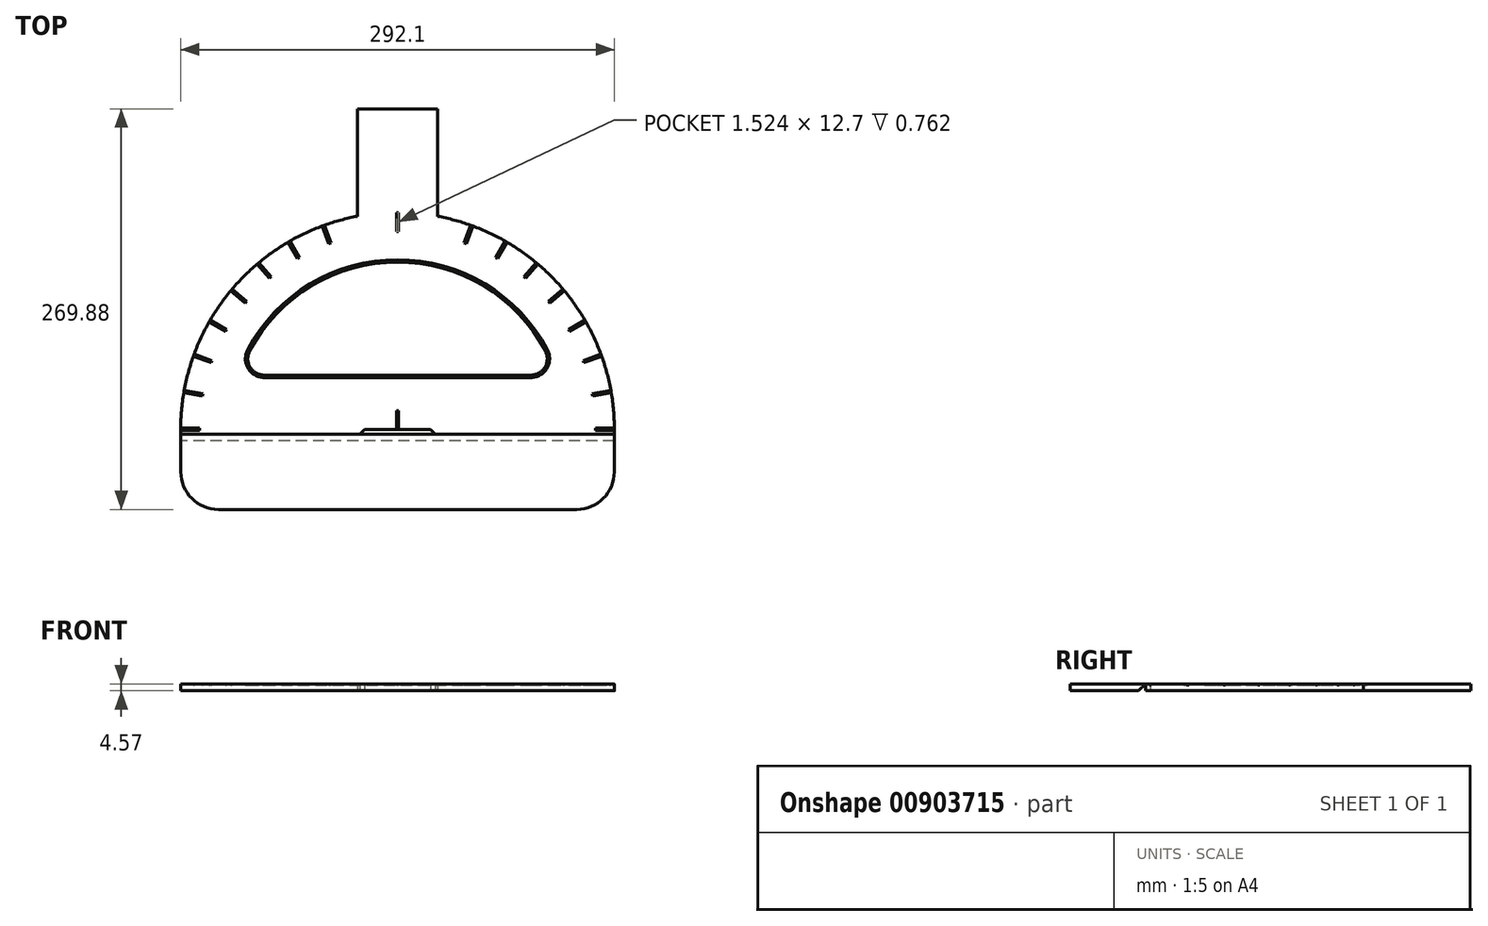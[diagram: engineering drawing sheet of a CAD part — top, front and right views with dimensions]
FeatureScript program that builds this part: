
annotation { "Feature Type Name" : "Feature", "Feature Type Description" : "" }
export const myFeature = defineFeature(function(context is Context, id is Id, definition is map)
    precondition{}
    {
        {
            var Q0;
            Q0=qCreatedBy(makeId("Top.planeOp"),FACE);
            var sketch = newSketch(context, id + "F0", { "sketchPlane" : qUnion([Q0])});
            skArc(sketch, "E0", {"start": v(146.02, -3.17) * mm, "mid": v(113.44, 92) * mm, "end": v(27.05, 143.52) * mm});
            skLineSegment(sketch, "E1", {"start": v(-146.02, -3.18) * mm, "end": v(-25.4, -3.18) * mm});
            skLineSegment(sketch, "E2", {"start": v(-25.4, -3.18) * mm, "end": v(-22.22, 0) * mm});
            skLineSegment(sketch, "E3", {"start": v(0, 4.34) * mm, "end": v(0, -10.16) * mm, "construction": true});
            skLineSegment(sketch, "E4.MirrorCS", {"start": v(25.4, -3.18) * mm, "end": v(22.22, 0) * mm});
            skLineSegment(sketch, "E5", {"start": v(-22.22, 0) * mm, "end": v(22.22, 0) * mm});
            skLineSegment(sketch, "E6.trimOffspring", {"start": v(25.4, -3.18) * mm, "end": v(146.02, -3.18) * mm});
            skLineSegment(sketch, "E7", {"start": v(0, 220.1) * mm, "end": v(0, 0) * mm, "construction": true});
            skLineSegment(sketch, "E8.bottom", {"start": v(-27.05, 215.9) * mm, "end": v(27.05, 215.9) * mm});
            skLineSegment(sketch, "E8.left", {"start": v(-27.05, 215.9) * mm, "end": v(-27.05, 143.52) * mm});
            skLineSegment(sketch, "E8.right", {"start": v(27.05, 215.9) * mm, "end": v(27.05, 143.52) * mm});
            skArc(sketch, "E9.trimOffspring", {"start": v(-27.05, 143.52) * mm, "mid": v(-113.44, 92) * mm, "end": v(-146.02, -3.17) * mm});
            skSolve(sketch);
        }
        {
            var Q0;
            Q0 = qSketchRegion(id + "F0", true);
            extrude(context, id + "F1", {"entities" : qUnion([Q0]), "depth" : 4.57 * mm, "offsetDistance" : 25.4 * mm});
        }
        {
            var Q0;
            Q0=makeQuery(id+"F1.opExtrude","CAP_FACE",FACE,{"disambiguationData":[OSD([sQuery(id+"F0.wireOp",EDGE,"E0"),sQuery(id+"F0.wireOp",EDGE,"E1")])],"isStart":false});
            var sketch = newSketch(context, id + "F2", { "sketchPlane" : qUnion([Q0])});
            skLineSegment(sketch, "E10", {"start": v(-89.75, 34.92) * mm, "end": v(89.75, 34.92) * mm});
            skArc(sketch, "E11.0", {"start": v(100.96, 53.58) * mm, "mid": v(0, 114.3) * mm, "end": v(-100.96, 53.58) * mm});
            skArc(sketch, "E12.filletArc", {"start": v(-100.96, 53.58) * mm, "mid": v(-100.63, 41.08) * mm, "end": v(-89.75, 34.92) * mm});
            skArc(sketch, "E13.filletArc", {"start": v(89.75, 34.92) * mm, "mid": v(100.63, 41.08) * mm, "end": v(100.96, 53.58) * mm});
            skArc(sketch, "E14.0", {"start": v(99.55, 52.83) * mm, "mid": v(0, 112.7) * mm, "end": v(-99.55, 52.83) * mm});
            skArc(sketch, "E14.1", {"start": v(89.75, 36.53) * mm, "mid": v(99.26, 41.9) * mm, "end": v(99.55, 52.83) * mm});
            skLineSegment(sketch, "E14.2", {"start": v(-89.75, 36.53) * mm, "end": v(89.75, 36.53) * mm});
            skArc(sketch, "E14.3", {"start": v(-99.55, 52.83) * mm, "mid": v(-99.26, 41.9) * mm, "end": v(-89.75, 36.53) * mm});
            skLineSegment(sketch, "E15.0", {"start": v(-133.35, -0.76) * mm, "end": v(-146.05, -0.76) * mm});
            skLineSegment(sketch, "E16", {"start": v(-146.05, -0.76) * mm, "end": v(-146.05, 0.76) * mm});
            skLineSegment(sketch, "E17.0", {"start": v(-133.35, -0.76) * mm, "end": v(-133.35, 0.76) * mm});
            skLineSegment(sketch, "E18.trimOffspring", {"start": v(-133.35, 0.76) * mm, "end": v(-146.05, 0.76) * mm});
            skLineSegment(sketch, "E19", {"start": v(0, 161.97) * mm, "end": v(0, 0) * mm, "construction": true});
            skLineSegment(sketch, "E20", {"start": v(-0.76, 0) * mm, "end": v(0.76, 0) * mm});
            skLineSegment(sketch, "E21", {"start": v(-0.76, 12.7) * mm, "end": v(0.76, 12.7) * mm});
            skLineSegment(sketch, "E22.trimOffspring", {"start": v(-0.76, 12.7) * mm, "end": v(-0.76, 0) * mm});
            skLineSegment(sketch, "E23.trimOffspring", {"start": v(0.76, 12.7) * mm, "end": v(0.76, 0) * mm});
            skLineSegment(sketch, "E24", {"start": v(0.76, 0) * mm, "end": v(-161.31, 0) * mm, "construction": true});
            skLineSegment(sketch, "E25.1.0", {"start": v(0.75, -0.13) * mm, "end": v(-158.86, 28.01) * mm, "construction": true});
            skLineSegment(sketch, "E25.1.1", {"start": v(-131.46, 22.4) * mm, "end": v(-143.96, 24.61) * mm});
            skLineSegment(sketch, "E25.1.2", {"start": v(-131.2, 23.9) * mm, "end": v(-143.7, 26.11) * mm});
            skLineSegment(sketch, "E25.1.3", {"start": v(-131.46, 22.4) * mm, "end": v(-131.2, 23.9) * mm});
            skLineSegment(sketch, "E25.1.4", {"start": v(-143.96, 24.61) * mm, "end": v(-143.7, 26.11) * mm});
            skLineSegment(sketch, "E25.2.0", {"start": v(0.72, -0.26) * mm, "end": v(-151.59, 55.17) * mm, "construction": true});
            skLineSegment(sketch, "E25.2.1", {"start": v(-125.57, 44.9) * mm, "end": v(-137.5, 49.24) * mm});
            skLineSegment(sketch, "E25.2.2", {"start": v(-125.05, 46.32) * mm, "end": v(-136.98, 50.67) * mm});
            skLineSegment(sketch, "E25.2.3", {"start": v(-125.57, 44.9) * mm, "end": v(-125.05, 46.32) * mm});
            skLineSegment(sketch, "E25.2.4", {"start": v(-137.5, 49.24) * mm, "end": v(-136.98, 50.67) * mm});
            skLineSegment(sketch, "E25.3.0", {"start": v(0.66, -0.38) * mm, "end": v(-139.7, 80.66) * mm, "construction": true});
            skLineSegment(sketch, "E25.3.1", {"start": v(-115.87, 66.02) * mm, "end": v(-126.86, 72.37) * mm});
            skLineSegment(sketch, "E25.3.2", {"start": v(-115.1, 67.33) * mm, "end": v(-126.1, 73.68) * mm});
            skLineSegment(sketch, "E25.3.3", {"start": v(-115.87, 66.02) * mm, "end": v(-115.1, 67.33) * mm});
            skLineSegment(sketch, "E25.3.4", {"start": v(-126.86, 72.37) * mm, "end": v(-126.1, 73.68) * mm});
            skLineSegment(sketch, "E25.4.0", {"start": v(0.58, -0.49) * mm, "end": v(-123.57, 103.7) * mm, "construction": true});
            skLineSegment(sketch, "E25.4.1", {"start": v(-102.64, 85.13) * mm, "end": v(-112.37, 93.3) * mm});
            skLineSegment(sketch, "E25.4.2", {"start": v(-101.66, 86.3) * mm, "end": v(-111.4, 94.46) * mm});
            skLineSegment(sketch, "E25.4.3", {"start": v(-102.64, 85.13) * mm, "end": v(-101.66, 86.3) * mm});
            skLineSegment(sketch, "E25.4.4", {"start": v(-112.37, 93.3) * mm, "end": v(-111.4, 94.46) * mm});
            skLineSegment(sketch, "E25.5.0", {"start": v(0.49, -0.58) * mm, "end": v(-103.7, 123.57) * mm, "construction": true});
            skLineSegment(sketch, "E25.5.1", {"start": v(-86.3, 101.66) * mm, "end": v(-94.46, 111.4) * mm});
            skLineSegment(sketch, "E25.5.2", {"start": v(-85.13, 102.64) * mm, "end": v(-93.3, 112.37) * mm});
            skLineSegment(sketch, "E25.5.3", {"start": v(-86.3, 101.66) * mm, "end": v(-85.13, 102.64) * mm});
            skLineSegment(sketch, "E25.5.4", {"start": v(-94.46, 111.4) * mm, "end": v(-93.3, 112.37) * mm});
            skLineSegment(sketch, "E25.6.0", {"start": v(0.38, -0.66) * mm, "end": v(-80.66, 139.7) * mm, "construction": true});
            skLineSegment(sketch, "E25.6.1", {"start": v(-67.33, 115.1) * mm, "end": v(-73.68, 126.1) * mm});
            skLineSegment(sketch, "E25.6.2", {"start": v(-66.02, 115.87) * mm, "end": v(-72.37, 126.86) * mm});
            skLineSegment(sketch, "E25.6.3", {"start": v(-67.33, 115.1) * mm, "end": v(-66.02, 115.87) * mm});
            skLineSegment(sketch, "E25.6.4", {"start": v(-73.68, 126.1) * mm, "end": v(-72.37, 126.86) * mm});
            skLineSegment(sketch, "E25.7.0", {"start": v(0.26, -0.72) * mm, "end": v(-55.17, 151.59) * mm, "construction": true});
            skLineSegment(sketch, "E25.7.1", {"start": v(-46.32, 125.05) * mm, "end": v(-50.67, 136.98) * mm});
            skLineSegment(sketch, "E25.7.2", {"start": v(-44.9, 125.57) * mm, "end": v(-49.24, 137.5) * mm});
            skLineSegment(sketch, "E25.7.3", {"start": v(-46.32, 125.05) * mm, "end": v(-44.9, 125.57) * mm});
            skLineSegment(sketch, "E25.7.4", {"start": v(-50.67, 136.98) * mm, "end": v(-49.24, 137.5) * mm});
            skLineSegment(sketch, "E25.8.0", {"start": v(0.13, -0.75) * mm, "end": v(-28.01, 158.86) * mm, "construction": true});
            skLineSegment(sketch, "E25.9.0", {"start": v(0, -0.76) * mm, "end": v(0, 161.31) * mm, "construction": true});
            skLineSegment(sketch, "E25.9.1", {"start": v(-0.76, 133.35) * mm, "end": v(-0.76, 146.05) * mm});
            skLineSegment(sketch, "E25.9.2", {"start": v(0.76, 133.35) * mm, "end": v(0.76, 146.05) * mm});
            skLineSegment(sketch, "E25.9.3", {"start": v(-0.76, 133.35) * mm, "end": v(0.76, 133.35) * mm});
            skLineSegment(sketch, "E25.9.4", {"start": v(-0.76, 146.05) * mm, "end": v(0.76, 146.05) * mm});
            skLineSegment(sketch, "E25.10.0", {"start": v(-0.13, -0.75) * mm, "end": v(28.01, 158.86) * mm, "construction": true});
            skLineSegment(sketch, "E25.11.0", {"start": v(-0.26, -0.72) * mm, "end": v(55.17, 151.59) * mm, "construction": true});
            skLineSegment(sketch, "E25.11.1", {"start": v(44.9, 125.57) * mm, "end": v(49.24, 137.5) * mm});
            skLineSegment(sketch, "E25.11.2", {"start": v(46.32, 125.05) * mm, "end": v(50.67, 136.98) * mm});
            skLineSegment(sketch, "E25.11.3", {"start": v(44.9, 125.57) * mm, "end": v(46.32, 125.05) * mm});
            skLineSegment(sketch, "E25.11.4", {"start": v(49.24, 137.5) * mm, "end": v(50.67, 136.98) * mm});
            skLineSegment(sketch, "E25.12.0", {"start": v(-0.38, -0.66) * mm, "end": v(80.66, 139.7) * mm, "construction": true});
            skLineSegment(sketch, "E25.12.1", {"start": v(66.02, 115.87) * mm, "end": v(72.37, 126.86) * mm});
            skLineSegment(sketch, "E25.12.2", {"start": v(67.33, 115.1) * mm, "end": v(73.68, 126.1) * mm});
            skLineSegment(sketch, "E25.12.3", {"start": v(66.02, 115.87) * mm, "end": v(67.33, 115.1) * mm});
            skLineSegment(sketch, "E25.12.4", {"start": v(72.37, 126.86) * mm, "end": v(73.68, 126.1) * mm});
            skLineSegment(sketch, "E25.13.0", {"start": v(-0.49, -0.58) * mm, "end": v(103.7, 123.57) * mm, "construction": true});
            skLineSegment(sketch, "E25.13.1", {"start": v(85.13, 102.64) * mm, "end": v(93.3, 112.37) * mm});
            skLineSegment(sketch, "E25.13.2", {"start": v(86.3, 101.66) * mm, "end": v(94.46, 111.4) * mm});
            skLineSegment(sketch, "E25.13.3", {"start": v(85.13, 102.64) * mm, "end": v(86.3, 101.66) * mm});
            skLineSegment(sketch, "E25.13.4", {"start": v(93.3, 112.37) * mm, "end": v(94.46, 111.4) * mm});
            skLineSegment(sketch, "E25.14.0", {"start": v(-0.58, -0.49) * mm, "end": v(123.57, 103.7) * mm, "construction": true});
            skLineSegment(sketch, "E25.14.1", {"start": v(101.66, 86.3) * mm, "end": v(111.4, 94.46) * mm});
            skLineSegment(sketch, "E25.14.2", {"start": v(102.64, 85.13) * mm, "end": v(112.37, 93.3) * mm});
            skLineSegment(sketch, "E25.14.3", {"start": v(101.66, 86.3) * mm, "end": v(102.64, 85.13) * mm});
            skLineSegment(sketch, "E25.14.4", {"start": v(111.4, 94.46) * mm, "end": v(112.37, 93.3) * mm});
            skLineSegment(sketch, "E25.15.0", {"start": v(-0.66, -0.38) * mm, "end": v(139.7, 80.66) * mm, "construction": true});
            skLineSegment(sketch, "E25.15.1", {"start": v(115.1, 67.33) * mm, "end": v(126.1, 73.68) * mm});
            skLineSegment(sketch, "E25.15.2", {"start": v(115.87, 66.02) * mm, "end": v(126.86, 72.37) * mm});
            skLineSegment(sketch, "E25.15.3", {"start": v(115.1, 67.33) * mm, "end": v(115.87, 66.02) * mm});
            skLineSegment(sketch, "E25.15.4", {"start": v(126.1, 73.68) * mm, "end": v(126.86, 72.37) * mm});
            skLineSegment(sketch, "E25.16.0", {"start": v(-0.72, -0.26) * mm, "end": v(151.59, 55.17) * mm, "construction": true});
            skLineSegment(sketch, "E25.16.1", {"start": v(125.05, 46.32) * mm, "end": v(136.98, 50.67) * mm});
            skLineSegment(sketch, "E25.16.2", {"start": v(125.57, 44.9) * mm, "end": v(137.5, 49.24) * mm});
            skLineSegment(sketch, "E25.16.3", {"start": v(125.05, 46.32) * mm, "end": v(125.57, 44.9) * mm});
            skLineSegment(sketch, "E25.16.4", {"start": v(136.98, 50.67) * mm, "end": v(137.5, 49.24) * mm});
            skLineSegment(sketch, "E25.17.0", {"start": v(-0.75, -0.13) * mm, "end": v(158.86, 28.01) * mm, "construction": true});
            skLineSegment(sketch, "E25.17.1", {"start": v(131.2, 23.9) * mm, "end": v(143.7, 26.11) * mm});
            skLineSegment(sketch, "E25.17.2", {"start": v(131.46, 22.4) * mm, "end": v(143.96, 24.61) * mm});
            skLineSegment(sketch, "E25.17.3", {"start": v(131.2, 23.9) * mm, "end": v(131.46, 22.4) * mm});
            skLineSegment(sketch, "E25.17.4", {"start": v(143.7, 26.11) * mm, "end": v(143.96, 24.61) * mm});
            skLineSegment(sketch, "E25.18.0", {"start": v(-0.76, 0) * mm, "end": v(161.31, 0) * mm, "construction": true});
            skLineSegment(sketch, "E25.18.1", {"start": v(133.35, 0.76) * mm, "end": v(146.05, 0.76) * mm});
            skLineSegment(sketch, "E25.18.2", {"start": v(133.35, -0.76) * mm, "end": v(146.05, -0.76) * mm});
            skLineSegment(sketch, "E25.18.3", {"start": v(133.35, 0.76) * mm, "end": v(133.35, -0.76) * mm});
            skLineSegment(sketch, "E25.18.4", {"start": v(146.05, 0.76) * mm, "end": v(146.05, -0.76) * mm});
            skLineSegment(sketch, "E25.anchor1", {"start": v(0, 0) * mm, "end": v(-161.31, 0) * mm, "construction": true});
            skLineSegment(sketch, "E25.anchor2", {"start": v(0, 0) * mm, "end": v(161.31, 0) * mm, "construction": true});
            skSolve(sketch);
        }
        {
            var Q0;
            Q0 = qSketchRegion(id + "F2", true);
            extrude(context, id + "F3", {"entities" : qUnion([Q0]), "operationType" : NewBodyOperationType.REMOVE, "oppositeDirection" : true, "depth" : 0.76 * mm, "offsetDistance" : 25.4 * mm});
        }
        {
            var Q0;
            Q0=qCreatedBy(makeId("Top.planeOp"),FACE);
            var sketch = newSketch(context, id + "F4", { "sketchPlane" : qUnion([Q0])});
            skLineSegment(sketch, "E26.bottom", {"start": v(146.02, -3.17) * mm, "end": v(146.02, -3.17) * mm});
            skLineSegment(sketch, "E26.top", {"start": v(-120.62, -53.97) * mm, "end": v(120.62, -53.97) * mm});
            skLineSegment(sketch, "E26.left", {"start": v(146.02, -3.17) * mm, "end": v(146.02, -28.57) * mm});
            skLineSegment(sketch, "E26.right", {"start": v(-146.02, -3.17) * mm, "end": v(-146.02, -28.57) * mm});
            skArc(sketch, "E27.filletArc", {"start": v(-146.02, -28.58) * mm, "mid": v(-138.58, -46.54) * mm, "end": v(-120.62, -53.98) * mm});
            skArc(sketch, "E28.filletArc", {"start": v(120.62, -53.97) * mm, "mid": v(138.58, -46.54) * mm, "end": v(146.02, -28.57) * mm});
            skLineSegment(sketch, "E29", {"start": v(0, 0) * mm, "end": v(0, -87.96) * mm, "construction": true});
            skLineSegment(sketch, "E30", {"start": v(-146.02, -3.17) * mm, "end": v(146.02, -3.17) * mm});
            skSolve(sketch);
        }
        {
            var Q0;
            Q0 = qSketchRegion(id + "F4", true);
            extrude(context, id + "F5", {"entities" : qUnion([Q0]), "operationType" : NewBodyOperationType.ADD, "depth" : 4.57 * mm, "offsetDistance" : 25.4 * mm});
        }
        {
            var Q0;
            Q0=qCreatedBy(makeId("Right.planeOp"),FACE);
            var sketch = newSketch(context, id + "F6", { "sketchPlane" : qUnion([Q0])});
            skLineSegment(sketch, "E31", {"start": v(-3.17, 4.57) * mm, "end": v(-3.17, 0) * mm});
            skLineSegment(sketch, "E32", {"start": v(-3.17, 0) * mm, "end": v(-7.75, 0) * mm});
            skLineSegment(sketch, "E33", {"start": v(-7.75, 0) * mm, "end": v(-3.17, 4.57) * mm});
            skSolve(sketch);
        }
        {
            var Q0;
            Q0 = qSketchRegion(id + "F6", true);
            extrude(context, id + "F7", {"entities" : qUnion([Q0]), "operationType" : NewBodyOperationType.REMOVE, "endBound" : BoundingType.SYMMETRIC, "depth" : 304.8 * mm, "offsetDistance" : 25.4 * mm});
        }
    });
